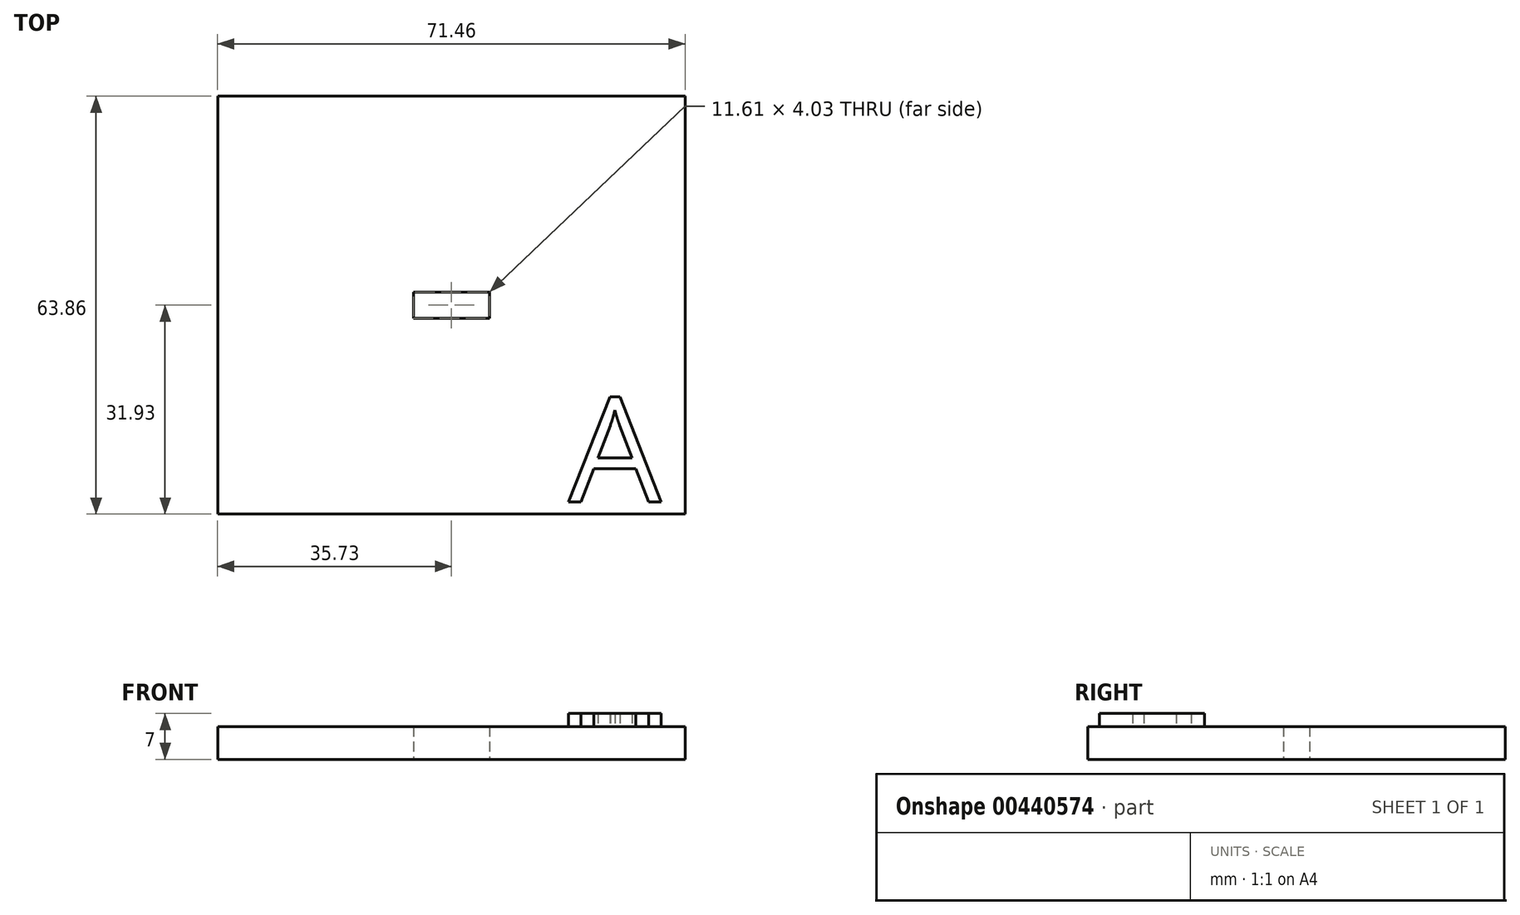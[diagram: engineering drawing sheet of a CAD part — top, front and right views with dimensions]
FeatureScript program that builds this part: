
annotation { "Feature Type Name" : "Feature", "Feature Type Description" : "" }
export const myFeature = defineFeature(function(context is Context, id is Id, definition is map)
    precondition{}
    {
        {
            var Q0;
            Q0=qCreatedBy(makeId("Top.planeOp"),FACE);
            var sketch = newSketch(context, id + "F0", { "sketchPlane" : qUnion([Q0])});
            skLineSegment(sketch, "E0.bottom", {"start": v(-35.73, 31.93) * mm, "end": v(35.73, 31.93) * mm});
            skLineSegment(sketch, "E0.top", {"start": v(-35.73, -31.93) * mm, "end": v(35.73, -31.93) * mm});
            skLineSegment(sketch, "E0.left", {"start": v(-35.73, 31.93) * mm, "end": v(-35.73, -31.93) * mm});
            skLineSegment(sketch, "E0.right", {"start": v(35.73, 31.93) * mm, "end": v(35.73, -31.93) * mm});
            skPoint(sketch, "E0.middle", {"position": v(0, 0) * mm});
            skLineSegment(sketch, "E1.0", {"start": v(-5.8, 2.01) * mm, "end": v(5.8, 2.01) * mm});
            skLineSegment(sketch, "E1.1", {"start": v(-5.8, 2.01) * mm, "end": v(-5.8, -2.01) * mm});
            skLineSegment(sketch, "E1.2", {"start": v(-5.8, -2.01) * mm, "end": v(5.8, -2.01) * mm});
            skLineSegment(sketch, "E1.3", {"start": v(5.8, 2.01) * mm, "end": v(5.8, -2.01) * mm});
            skSolve(sketch);
        }
        {
            var Q0;
            Q0 = qSketchRegion(id + "F0", true);
            extrude(context, id + "F1", {"entities" : qUnion([Q0]), "depth" : 5 * mm});
        }
        {
            var Q0;
            Q0=makeQuery(id+"F1.opExtrude","CAP_FACE",FACE,{"disambiguationData":[OSD([sQuery(id+"F0.wireOp",EDGE,"E0.bottom"),sQuery(id+"F0.wireOp",EDGE,"E0.top"),sQuery(id+"F0.wireOp",EDGE,"E0.left"),sQuery(id+"F0.wireOp",EDGE,"E0.right"),sQuery(id+"F0.wireOp",EDGE,"E1.0"),sQuery(id+"F0.wireOp",EDGE,"E1.1"),sQuery(id+"F0.wireOp",EDGE,"E1.2"),sQuery(id+"F0.wireOp",EDGE,"E1.3")])],"isStart":false});
            var sketch = newSketch(context, id + "F2", { "sketchPlane" : qUnion([Q0])});
            skText(sketch, "E2", { "text": "A", "fontName": "OpenSans-Regular.ttf"});
            const initialGuessF2  = {"E2": [0.0179, -0.03011, 1, 0, 0.01614]};
            skSetInitialGuess(sketch, initialGuessF2);
            skSolve(sketch);
        }
        {
            var Q0;
            Q0 = qSketchRegion(id + "F2", true);
            extrude(context, id + "F3", {"entities" : qUnion([Q0]), "operationType" : NewBodyOperationType.ADD, "depth" : 2 * mm});
        }
    });
